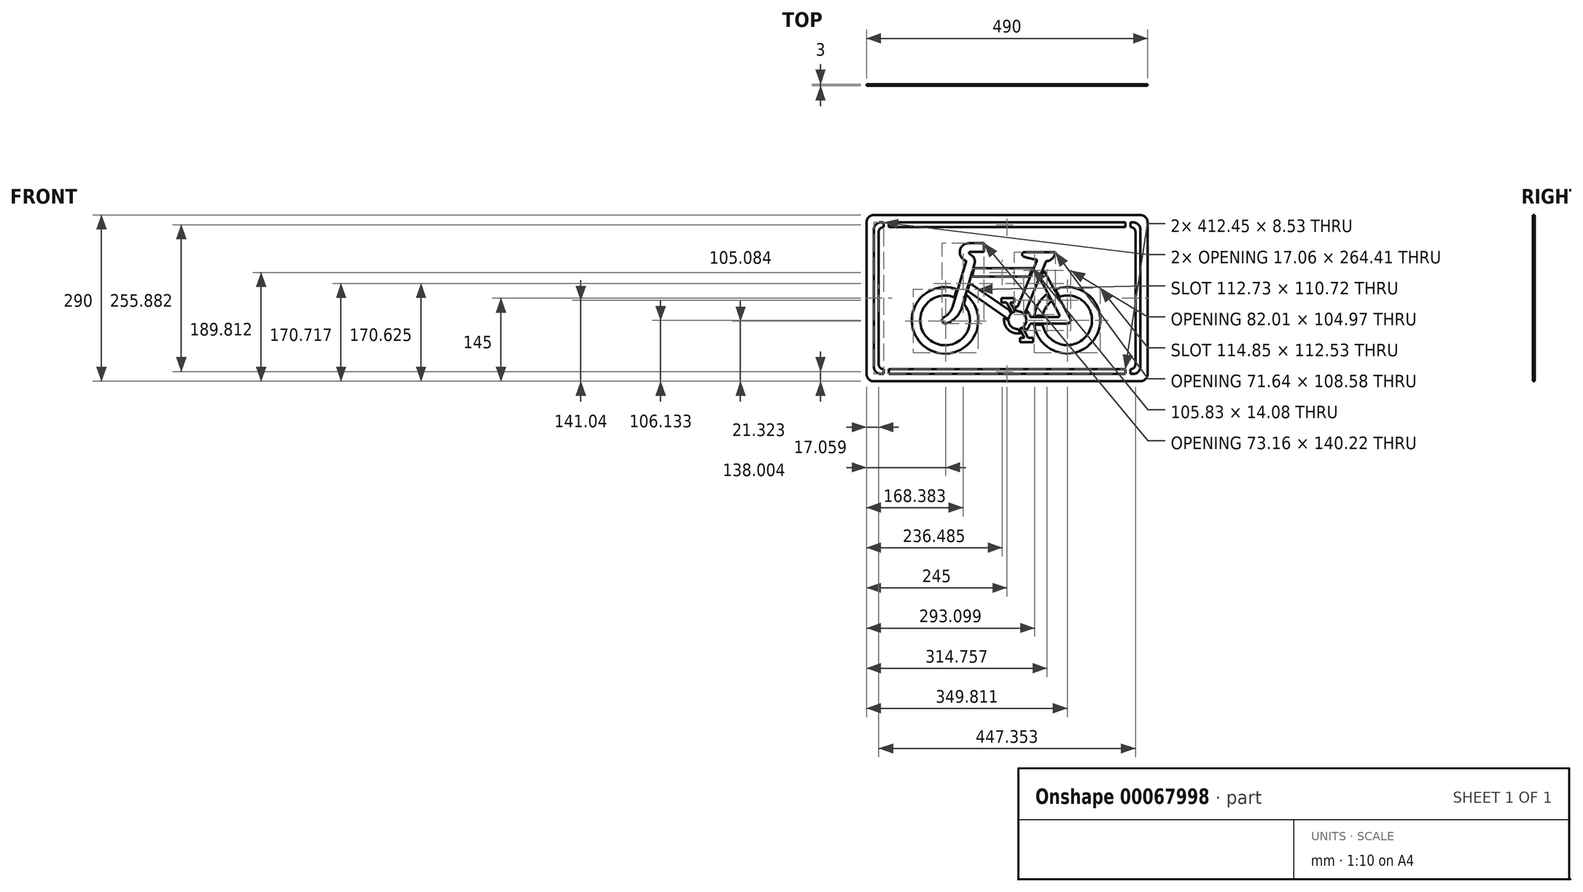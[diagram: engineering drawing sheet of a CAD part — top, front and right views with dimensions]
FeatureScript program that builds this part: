
annotation { "Feature Type Name" : "Feature", "Feature Type Description" : "" }
export const myFeature = defineFeature(function(context is Context, id is Id, definition is map)
    precondition{}
    {
        {
            var Q0;
            Q0=qCreatedBy(makeId("Front.planeOp"),FACE);
            var sketch = newSketch(context, id + "F0", { "sketchPlane" : qUnion([Q0])});
            skLineSegment(sketch, "E0", {"start": v(-245, -131.62) * mm, "end": v(-245, 131.62) * mm});
            skArc(sketch, "E1", {"start": v(-231.62, -145) * mm, "mid": v(-241.08, -141.08) * mm, "end": v(-245, -131.62) * mm});
            skLineSegment(sketch, "E2", {"start": v(231.62, -145) * mm, "end": v(-231.62, -145) * mm});
            skArc(sketch, "E3", {"start": v(245, -131.62) * mm, "mid": v(241.08, -141.08) * mm, "end": v(231.62, -145) * mm});
            skLineSegment(sketch, "E4", {"start": v(245, 131.62) * mm, "end": v(245, -131.62) * mm});
            skArc(sketch, "E5", {"start": v(231.62, 145) * mm, "mid": v(241.08, 141.08) * mm, "end": v(245, 131.62) * mm});
            skLineSegment(sketch, "E6", {"start": v(-231.62, 145) * mm, "end": v(231.62, 145) * mm});
            skArc(sketch, "E7", {"start": v(-245, 131.62) * mm, "mid": v(-241.08, 141.08) * mm, "end": v(-231.62, 145) * mm});
            skArc(sketch, "E8", {"start": v(-87.61, 15.44) * mm, "mid": v(-137.3, -88.64) * mm, "end": v(-70.76, 5.57) * mm});
            skLineSegment(sketch, "E9", {"start": v(-87.61, 15.44) * mm, "end": v(-91.77, 1.5) * mm});
            skArc(sketch, "E10", {"start": v(-91.77, 1.5) * mm, "mid": v(-133.2, -74.03) * mm, "end": v(-75.33, -10.22) * mm});
            skLineSegment(sketch, "E11", {"start": v(-70.76, 5.57) * mm, "end": v(-75.33, -10.22) * mm});
            skLineSegment(sketch, "E12", {"start": v(-1.21, -7.66) * mm, "end": v(8.93, -25.71) * mm});
            skLineSegment(sketch, "E13", {"start": v(-1.21, -7.66) * mm, "end": v(-9.8, -7.66) * mm});
            skLineSegment(sketch, "E14", {"start": v(-9.8, -7.66) * mm, "end": v(-9.8, 0.15) * mm});
            skLineSegment(sketch, "E15", {"start": v(-9.8, 0.15) * mm, "end": v(12.75, 0.15) * mm});
            skLineSegment(sketch, "E16", {"start": v(12.75, 0.15) * mm, "end": v(12.75, -7.66) * mm});
            skLineSegment(sketch, "E17", {"start": v(5.77, -7.66) * mm, "end": v(12.75, -7.66) * mm});
            skLineSegment(sketch, "E18", {"start": v(5.77, -7.66) * mm, "end": v(14.05, -23.3) * mm});
            skArc(sketch, "E19", {"start": v(14.05, -23.3) * mm, "mid": v(11.38, -24.27) * mm, "end": v(8.93, -25.71) * mm});
            skLineSegment(sketch, "E20", {"start": v(57.5, 33.6) * mm, "end": v(90.98, -29.24) * mm});
            skLineSegment(sketch, "E21", {"start": v(63.62, 48.52) * mm, "end": v(57.5, 33.6) * mm});
            skLineSegment(sketch, "E22", {"start": v(110.02, -35.45) * mm, "end": v(63.62, 48.52) * mm});
            skArc(sketch, "E23", {"start": v(104.8, -44.31) * mm, "mid": v(109.93, -41.38) * mm, "end": v(110.02, -35.45) * mm});
            skLineSegment(sketch, "E24", {"start": v(40.34, -44.31) * mm, "end": v(104.8, -44.31) * mm});
            skArc(sketch, "E25", {"start": v(32.37, -56.44) * mm, "mid": v(37.33, -51.02) * mm, "end": v(40.34, -44.31) * mm});
            skLineSegment(sketch, "E26", {"start": v(32.37, -56.44) * mm, "end": v(28.75, -49.42) * mm});
            skArc(sketch, "E27", {"start": v(28.75, -49.42) * mm, "mid": v(33.31, -40.46) * mm, "end": v(31.4, -30.59) * mm});
            skLineSegment(sketch, "E28", {"start": v(34.78, -22.35) * mm, "end": v(31.4, -30.59) * mm});
            skArc(sketch, "E29", {"start": v(40.53, -33) * mm, "mid": v(38.36, -27.3) * mm, "end": v(34.78, -22.35) * mm});
            skLineSegment(sketch, "E30", {"start": v(88.73, -33) * mm, "end": v(40.53, -33) * mm});
            skArc(sketch, "E31", {"start": v(88.73, -33) * mm, "mid": v(90.92, -31.76) * mm, "end": v(90.98, -29.24) * mm});
            skArc(sketch, "E32", {"start": v(69.5, 7.29) * mm, "mid": v(54.58, -9.75) * mm, "end": v(47.36, -31.22) * mm});
            skLineSegment(sketch, "E33", {"start": v(69.5, 7.29) * mm, "end": v(76.44, -5.74) * mm});
            skArc(sketch, "E34", {"start": v(76.44, -5.74) * mm, "mid": v(67, -17.23) * mm, "end": v(62.02, -31.22) * mm});
            skLineSegment(sketch, "E35", {"start": v(62.02, -31.22) * mm, "end": v(47.36, -31.22) * mm});
            skArc(sketch, "E36", {"start": v(47.39, -46.1) * mm, "mid": v(154.3, -68.08) * mm, "end": v(83.97, 15.39) * mm});
            skLineSegment(sketch, "E37", {"start": v(47.39, -46.1) * mm, "end": v(62.06, -46.1) * mm});
            skArc(sketch, "E38", {"start": v(62.06, -46.1) * mm, "mid": v(141.82, -60.71) * mm, "end": v(91.07, 2.53) * mm});
            skLineSegment(sketch, "E39", {"start": v(91.07, 2.53) * mm, "end": v(83.97, 15.39) * mm});
            skLineSegment(sketch, "E40", {"start": v(-206.22, 123.68) * mm, "end": v(206.22, 123.68) * mm});
            skLineSegment(sketch, "E41", {"start": v(-206.22, 132.2) * mm, "end": v(-206.22, 123.68) * mm});
            skLineSegment(sketch, "E42", {"start": v(206.22, 132.2) * mm, "end": v(-206.22, 132.2) * mm});
            skLineSegment(sketch, "E43", {"start": v(206.22, 123.68) * mm, "end": v(206.22, 132.2) * mm});
            skLineSegment(sketch, "E44", {"start": v(2.51, -39.39) * mm, "end": v(-4.85, -34.26) * mm});
            skArc(sketch, "E45", {"start": v(2.51, -39.39) * mm, "mid": v(8.04, -50.2) * mm, "end": v(19.67, -53.7) * mm});
            skLineSegment(sketch, "E46", {"start": v(23.53, -60.79) * mm, "end": v(19.67, -53.7) * mm});
            skArc(sketch, "E47", {"start": v(-4.85, -34.26) * mm, "mid": v(2.15, -55.22) * mm, "end": v(23.53, -60.79) * mm});
            skLineSegment(sketch, "E48", {"start": v(-215.15, -123.68) * mm, "end": v(-215.15, -132.2) * mm});
            skLineSegment(sketch, "E49", {"start": v(-215.15, -132.2) * mm, "end": v(-219.41, -132.2) * mm});
            skArc(sketch, "E50", {"start": v(-219.41, -132.2) * mm, "mid": v(-228.46, -128.46) * mm, "end": v(-232.2, -119.41) * mm});
            skLineSegment(sketch, "E51", {"start": v(-232.2, -119.41) * mm, "end": v(-232.2, 119.41) * mm});
            skArc(sketch, "E52", {"start": v(-232.2, 119.41) * mm, "mid": v(-228.46, 128.46) * mm, "end": v(-219.41, 132.2) * mm});
            skLineSegment(sketch, "E53", {"start": v(-219.41, 132.2) * mm, "end": v(-215.15, 132.2) * mm});
            skLineSegment(sketch, "E54", {"start": v(-215.15, 132.2) * mm, "end": v(-215.15, 123.68) * mm});
            skArc(sketch, "E55", {"start": v(-215.15, 123.68) * mm, "mid": v(-221.18, 121.18) * mm, "end": v(-223.68, 115.15) * mm});
            skLineSegment(sketch, "E56", {"start": v(-223.68, 115.15) * mm, "end": v(-223.68, -115.15) * mm});
            skArc(sketch, "E57", {"start": v(-223.68, -115.15) * mm, "mid": v(-221.18, -121.18) * mm, "end": v(-215.15, -123.68) * mm});
            skLineSegment(sketch, "E58", {"start": v(215.15, -132.2) * mm, "end": v(215.15, -123.68) * mm});
            skArc(sketch, "E59", {"start": v(215.15, -123.68) * mm, "mid": v(221.18, -121.18) * mm, "end": v(223.68, -115.15) * mm});
            skLineSegment(sketch, "E60", {"start": v(223.68, -115.15) * mm, "end": v(223.68, 115.15) * mm});
            skArc(sketch, "E61", {"start": v(223.68, 115.15) * mm, "mid": v(221.18, 121.18) * mm, "end": v(215.15, 123.68) * mm});
            skLineSegment(sketch, "E62", {"start": v(215.15, 123.68) * mm, "end": v(215.15, 132.2) * mm});
            skLineSegment(sketch, "E63", {"start": v(215.15, 132.2) * mm, "end": v(219.41, 132.2) * mm});
            skArc(sketch, "E64", {"start": v(219.41, 132.2) * mm, "mid": v(228.46, 128.46) * mm, "end": v(232.2, 119.41) * mm});
            skLineSegment(sketch, "E65", {"start": v(232.2, 119.41) * mm, "end": v(232.2, -119.41) * mm});
            skArc(sketch, "E66", {"start": v(232.2, -119.41) * mm, "mid": v(228.46, -128.46) * mm, "end": v(219.41, -132.2) * mm});
            skLineSegment(sketch, "E67", {"start": v(219.41, -132.2) * mm, "end": v(215.15, -132.2) * mm});
            skLineSegment(sketch, "E68", {"start": v(-64.74, 26.33) * mm, "end": v(-68.72, 12.58) * mm});
            skLineSegment(sketch, "E69", {"start": v(-64.74, 26.33) * mm, "end": v(3.16, -20.48) * mm});
            skArc(sketch, "E70", {"start": v(3.58, -20.14) * mm, "mid": v(3.37, -20.3) * mm, "end": v(3.16, -20.48) * mm});
            skLineSegment(sketch, "E71", {"start": v(3.58, -20.14) * mm, "end": v(7.41, -26.96) * mm});
            skArc(sketch, "E72", {"start": v(7.41, -26.96) * mm, "mid": v(4.02, -31.54) * mm, "end": v(2.53, -37.04) * mm});
            skLineSegment(sketch, "E73", {"start": v(2.53, -37.04) * mm, "end": v(-68.72, 12.58) * mm});
            skArc(sketch, "E74", {"start": v(18.3, -15.13) * mm, "mid": v(15.27, -15.28) * mm, "end": v(12.28, -15.83) * mm});
            skLineSegment(sketch, "E75", {"start": v(18.3, -15.13) * mm, "end": v(51.82, 64.97) * mm});
            skArc(sketch, "E76", {"start": v(51.82, 64.97) * mm, "mid": v(51.77, 66.51) * mm, "end": v(50.49, 67.38) * mm});
            skArc(sketch, "E77", {"start": v(28.66, 72.54) * mm, "mid": v(39.43, 69.38) * mm, "end": v(50.49, 67.38) * mm});
            skArc(sketch, "E78", {"start": v(27.82, 79.54) * mm, "mid": v(26.3, 75.8) * mm, "end": v(28.66, 72.54) * mm});
            skArc(sketch, "E79", {"start": v(28.88, 79.92) * mm, "mid": v(28.32, 79.82) * mm, "end": v(27.82, 79.54) * mm});
            skLineSegment(sketch, "E80", {"start": v(28.88, 79.92) * mm, "end": v(83.07, 79.92) * mm});
            skArc(sketch, "E81", {"start": v(83.91, 78.95) * mm, "mid": v(83.71, 79.63) * mm, "end": v(83.07, 79.92) * mm});
            skArc(sketch, "E82", {"start": v(69.23, 64.6) * mm, "mid": v(79.04, 69.24) * mm, "end": v(83.91, 78.95) * mm});
            skArc(sketch, "E83", {"start": v(69.23, 64.6) * mm, "mid": v(68.37, 64.25) * mm, "end": v(67.82, 63.5) * mm});
            skLineSegment(sketch, "E84", {"start": v(67.82, 63.5) * mm, "end": v(30.1, -28.67) * mm});
            skArc(sketch, "E85", {"start": v(30.1, -28.67) * mm, "mid": v(23.82, -23.95) * mm, "end": v(16.03, -22.92) * mm});
            skLineSegment(sketch, "E86", {"start": v(12.28, -15.83) * mm, "end": v(16.03, -22.92) * mm});
            skLineSegment(sketch, "E87", {"start": v(-57.35, 51.85) * mm, "end": v(-61.43, 37.77) * mm});
            skLineSegment(sketch, "E88", {"start": v(-57.35, 51.85) * mm, "end": v(44.4, 51.85) * mm});
            skLineSegment(sketch, "E89", {"start": v(38.5, 37.77) * mm, "end": v(44.4, 51.85) * mm});
            skLineSegment(sketch, "E90", {"start": v(38.5, 37.77) * mm, "end": v(-61.43, 37.77) * mm});
            skArc(sketch, "E91", {"start": v(-66.4, 95.82) * mm, "mid": v(-82.15, 83.22) * mm, "end": v(-72.47, 65.52) * mm});
            skLineSegment(sketch, "E92", {"start": v(-66.4, 95.82) * mm, "end": v(-40.04, 95.82) * mm});
            skLineSegment(sketch, "E93", {"start": v(-40.04, 95.82) * mm, "end": v(-40.04, 80.63) * mm});
            skLineSegment(sketch, "E94", {"start": v(-40.04, 80.63) * mm, "end": v(-64.42, 80.63) * mm});
            skArc(sketch, "E95", {"start": v(-64.42, 80.63) * mm, "mid": v(-66.03, 79.5) * mm, "end": v(-65.52, 77.62) * mm});
            skLineSegment(sketch, "E96", {"start": v(-59.44, 72.53) * mm, "end": v(-65.52, 77.62) * mm});
            skArc(sketch, "E97", {"start": v(-56.93, 59.72) * mm, "mid": v(-56.4, 66.48) * mm, "end": v(-59.44, 72.53) * mm});
            skLineSegment(sketch, "E98", {"start": v(-56.93, 59.72) * mm, "end": v(-77.85, -12.52) * mm});
            skArc(sketch, "E99", {"start": v(-105.01, -43.93) * mm, "mid": v(-87.36, -31.75) * mm, "end": v(-77.85, -12.52) * mm});
            skArc(sketch, "E100", {"start": v(-111.05, -33.77) * mm, "mid": v(-112.45, -41.48) * mm, "end": v(-105.01, -43.93) * mm});
            skArc(sketch, "E101", {"start": v(-111.05, -33.77) * mm, "mid": v(-101.1, -25.9) * mm, "end": v(-94.8, -14.9) * mm});
            skLineSegment(sketch, "E102", {"start": v(-71.45, 63.44) * mm, "end": v(-94.8, -14.9) * mm});
            skArc(sketch, "E103", {"start": v(-71.45, 63.44) * mm, "mid": v(-71.55, 64.68) * mm, "end": v(-72.47, 65.52) * mm});
            skLineSegment(sketch, "E104", {"start": v(206.22, -123.68) * mm, "end": v(206.22, -132.2) * mm});
            skLineSegment(sketch, "E105", {"start": v(206.22, -132.2) * mm, "end": v(-206.22, -132.2) * mm});
            skLineSegment(sketch, "E106", {"start": v(-206.22, -132.2) * mm, "end": v(-206.22, -123.68) * mm});
            skLineSegment(sketch, "E107", {"start": v(-206.22, -123.68) * mm, "end": v(206.22, -123.68) * mm});
            skLineSegment(sketch, "E108", {"start": v(30.1, -68.8) * mm, "end": v(21.67, -53.34) * mm});
            skArc(sketch, "E109", {"start": v(21.67, -53.34) * mm, "mid": v(24.6, -52.3) * mm, "end": v(27.24, -50.7) * mm});
            skLineSegment(sketch, "E110", {"start": v(36.57, -68.8) * mm, "end": v(27.24, -50.7) * mm});
            skLineSegment(sketch, "E111", {"start": v(45.28, -68.8) * mm, "end": v(36.57, -68.8) * mm});
            skLineSegment(sketch, "E112", {"start": v(45.28, -76.61) * mm, "end": v(45.28, -68.8) * mm});
            skLineSegment(sketch, "E113", {"start": v(22.73, -76.61) * mm, "end": v(45.28, -76.61) * mm});
            skLineSegment(sketch, "E114", {"start": v(22.73, -68.8) * mm, "end": v(22.73, -76.61) * mm});
            skLineSegment(sketch, "E115", {"start": v(30.1, -68.8) * mm, "end": v(22.73, -68.8) * mm});
            skSolve(sketch);
        }
        {
            var Q0;
            Q0=makeQuery(id+"F0.imprint","IMPRINT",FACE,{"disambiguationData":[TD([[makeQuery(id+"F0.imprint","IMPRINT",EDGE,{"derivedFrom":sQuery(id+"F0.wireOp",EDGE,"E0")}),-1.0]])]});
            extrude(context, id + "F1", {"entities" : qUnion([Q0]), "depth" : 3 * mm});
        }
    });
